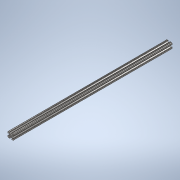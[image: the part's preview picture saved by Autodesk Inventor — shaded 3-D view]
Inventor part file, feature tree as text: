
AUTODESK INVENTOR PART (.ipt)
format: ipt  version: 2020 (Build 240168000, 168)  size: 243,200 bytes
history: native  units: in
note: dims shown in document units (in); Inventor stores cm internally (conversion verified against a paired STEP export)
features: extrude x1, sketch x1
ambient origin geometry x8: Origin, YZ Plane, XZ Plane, XY Plane, X Axis, Y Axis, Z Axis, Center Point
bodies: Solid1 (feature_tree)
feature tree (2):
  extrude  "Extrusion1"  [1 undecoded]
  sketch  "Sketch1"  dims[d0=28.0in d1=0.0in]
note: 1 required parameter value undecoded (feature->parameter linkage not recoverable at this tier; creation-order binding heuristic only, values carry confidence <= 0.55)
